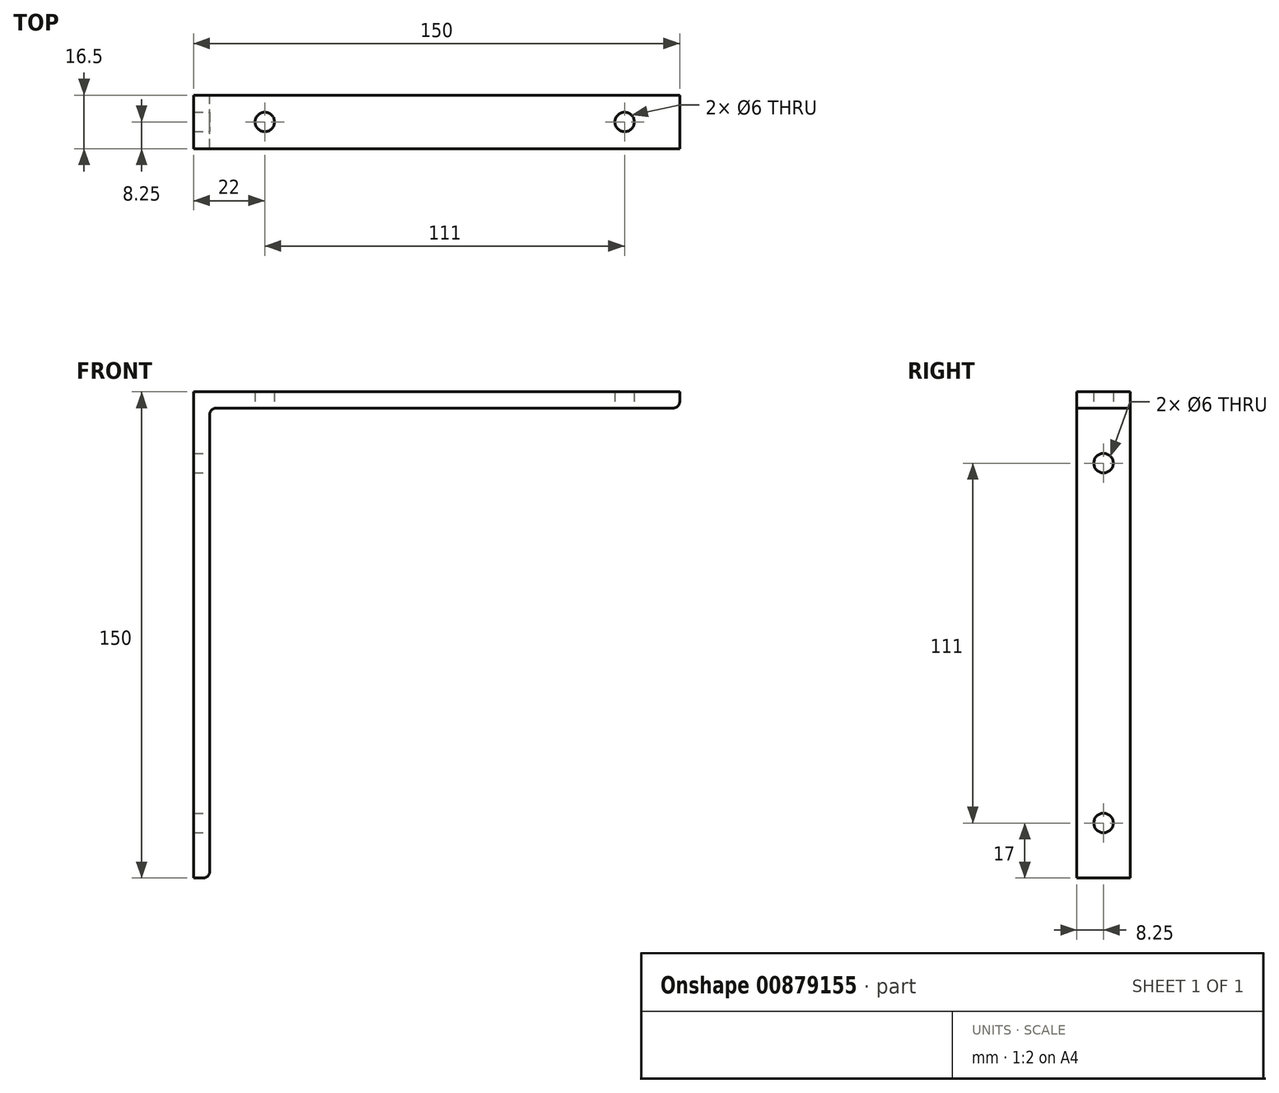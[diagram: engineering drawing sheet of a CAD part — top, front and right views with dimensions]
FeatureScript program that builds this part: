
annotation { "Feature Type Name" : "Feature", "Feature Type Description" : "" }
export const myFeature = defineFeature(function(context is Context, id is Id, definition is map)
    precondition{}
    {
        {
            var Q0;
            Q0=qCreatedBy(makeId("Front.planeOp"),FACE);
            var sketch = newSketch(context, id + "F0", { "sketchPlane" : qUnion([Q0])});
            skLineSegment(sketch, "E0.bottom", {"start": v(0, 0) * mm, "end": v(5, 0) * mm});
            skLineSegment(sketch, "E0.top", {"start": v(0, -150) * mm, "end": v(5, -150) * mm});
            skLineSegment(sketch, "E0.left", {"start": v(0, 0) * mm, "end": v(0, -150) * mm});
            skLineSegment(sketch, "E0.right", {"start": v(5, -5) * mm, "end": v(5, -150) * mm});
            skLineSegment(sketch, "E1.bottom", {"start": v(0, 0) * mm, "end": v(150, 0) * mm});
            skLineSegment(sketch, "E1.top", {"start": v(5, -5) * mm, "end": v(150, -5) * mm});
            skLineSegment(sketch, "E1.left", {"start": v(0, 0) * mm, "end": v(0, -5) * mm});
            skLineSegment(sketch, "E1.right", {"start": v(150, 0) * mm, "end": v(150, -5) * mm});
            skSolve(sketch);
        }
        {
            var Q0;
            Q0 = qSketchRegion(id + "F0", true);
            extrude(context, id + "F1", {"entities" : qUnion([Q0]), "depth" : 16.5 * mm, "offsetDistance" : 25 * mm});
        }
        {
            var Q0;
            Q0=makeQuery(id+"F1.opExtrude","SWEPT_EDGE",EDGE,{"disambiguationData":[OSD([sQuery(id+"F0.wireOp",EDGE,"E0.right"),sQuery(id+"F0.wireOp",EDGE,"E1.top")])]});
            var Q1;
            Q1=makeQuery(id+"F1.opExtrude","SWEPT_EDGE",EDGE,{"disambiguationData":[OSD([sQuery(id+"F0.wireOp",EDGE,"E1.top"),sQuery(id+"F0.wireOp",EDGE,"E1.right")])]});
            var Q2;
            Q2=makeQuery(id+"F1.opExtrude","SWEPT_EDGE",EDGE,{"disambiguationData":[OSD([sQuery(id+"F0.wireOp",EDGE,"E0.top"),sQuery(id+"F0.wireOp",EDGE,"E0.right")])]});
            fillet(context, id + "F2", {"entities" : qUnion([Q0, Q1, Q2]), "radius" : 2 * mm, "tangentPropagation" : true, "allowEdgeOverflow" : false});
        }
        {
            var Q0;
            Q0=makeQuery(id+"F1.opExtrude","SWEPT_FACE",FACE,{"disambiguationData":[OSD([sQuery(id+"F0.wireOp",EDGE,"E1.top")])]});
            var sketch = newSketch(context, id + "F3", { "sketchPlane" : qUnion([Q0])});
            skCircle(sketch, "E2", {"center": v(133, 8.25) * mm, "radius": 3 * mm});
            skPoint(sketch, "E2.centerSnap0", {"position": v(148, 8.25) * mm});
            skCircle(sketch, "E3", {"center": v(22, 8.25) * mm, "radius": 3 * mm});
            skPoint(sketch, "E3.centerSnap0", {"position": v(7, 8.25) * mm});
            skSolve(sketch);
        }
        {
            var Q0;
            Q0 = qSketchRegion(id + "F3", true);
            extrude(context, id + "F4", {"entities" : qUnion([Q0]), "operationType" : NewBodyOperationType.REMOVE, "oppositeDirection" : true, "depth" : 25 * mm, "offsetDistance" : 25 * mm});
        }
        {
            var Q0;
            Q0=makeQuery(id+"F1.opExtrude","SWEPT_FACE",FACE,{"disambiguationData":[OSD([sQuery(id+"F0.wireOp",EDGE,"E0.right")])]});
            var sketch = newSketch(context, id + "F5", { "sketchPlane" : qUnion([Q0])});
            skCircle(sketch, "E4", {"center": v(-8.25, -133) * mm, "radius": 3 * mm});
            skPoint(sketch, "E4.centerSnap0", {"position": v(-8.25, -148) * mm});
            skCircle(sketch, "E5", {"center": v(-8.25, -22) * mm, "radius": 3 * mm});
            skPoint(sketch, "E5.centerSnap0", {"position": v(-8.25, -7) * mm});
            skSolve(sketch);
        }
        {
            var Q0;
            Q0 = qSketchRegion(id + "F5", true);
            extrude(context, id + "F6", {"entities" : qUnion([Q0]), "operationType" : NewBodyOperationType.REMOVE, "oppositeDirection" : true, "depth" : 25 * mm, "offsetDistance" : 25 * mm});
        }
    });
